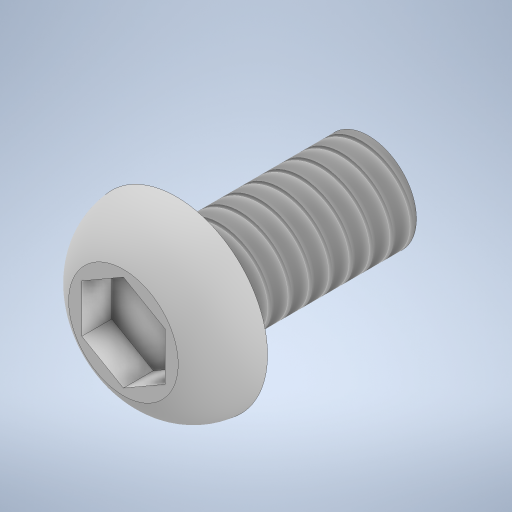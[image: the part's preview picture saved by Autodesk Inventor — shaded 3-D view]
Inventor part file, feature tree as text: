
AUTODESK INVENTOR PART (.ipt)
format: ipt  version: 2023.5 (Build 275446000, 446)  size: 309,248 bytes
history: native  units: in
note: dims shown in document units (in); Inventor stores cm internally (conversion verified against a paired STEP export)
features: sketch x3, extrude x2, thread x1, other x1, revolve x1
ambient origin geometry x8: Origin, YZ Plane, XZ Plane, XY Plane, X Axis, Y Axis, Z Axis, Center Point
bodies: Solid1 (feature_tree)
feature tree (8):
  extrude  "Extrusion1"  Depth=0.3937in TaperAngle=0.0deg
  thread  "Thread1"  [1 undecoded]
  other  "Work Axis1"
  revolve  "Revolution1"  [1 undecoded]
  extrude  "Extrusion2"  Depth=0.13in
  sketch  "Sketch1"  dims[d0=0.1969in d1=0.3937in d2=0.0in d3=0.394in d4=0.0in]
  sketch  "Sketch2"  dims[d5=0.187in d6=0.1083in]
  sketch  "Sketch3"  dims[d7=0.1122in d8=0.13in d9=90.0deg d10=0.0614in d11=0.0in]
note: 2 required parameter values undecoded (feature->parameter linkage not recoverable at this tier; creation-order binding heuristic only, values carry confidence <= 0.55)